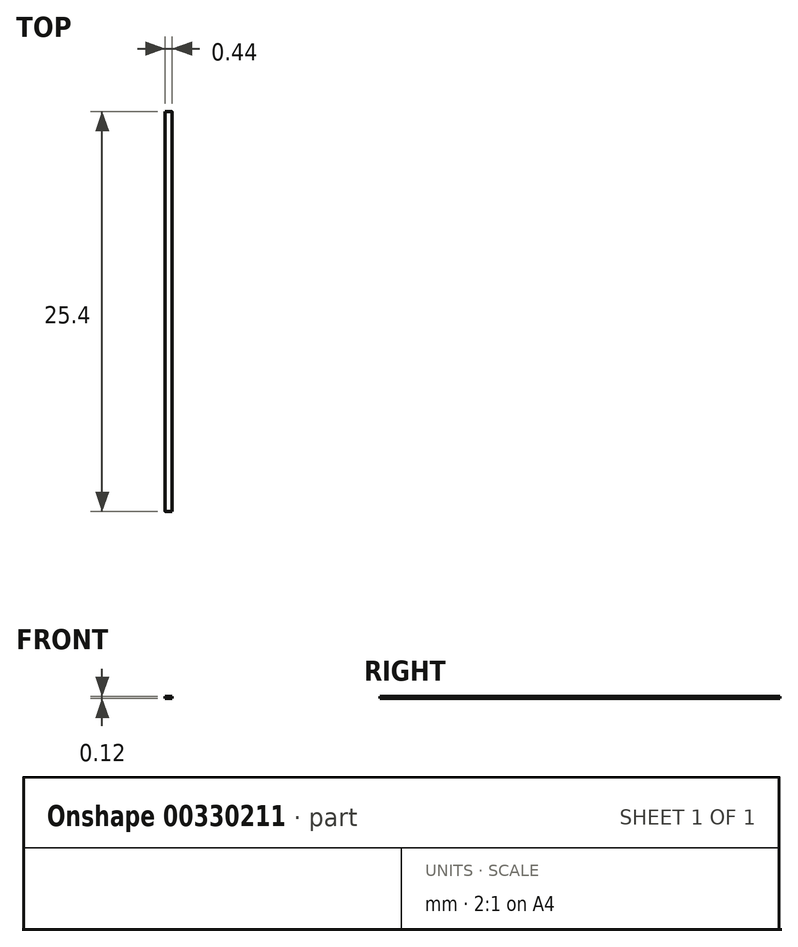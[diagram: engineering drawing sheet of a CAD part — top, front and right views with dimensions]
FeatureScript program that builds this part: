
annotation { "Feature Type Name" : "Feature", "Feature Type Description" : "" }
export const myFeature = defineFeature(function(context is Context, id is Id, definition is map)
    precondition{}
    {
        {
            var Q0;
            Q0=qCreatedBy(makeId("Front.planeOp"),FACE);
            var sketch = newSketch(context, id + "F0", { "sketchPlane" : qUnion([Q0])});
            skLineSegment(sketch, "E0.bottom", {"start": v(0.22, -0.06) * mm, "end": v(-0.22, -0.06) * mm});
            skLineSegment(sketch, "E0.top", {"start": v(0.22, 0.06) * mm, "end": v(-0.22, 0.06) * mm});
            skLineSegment(sketch, "E0.left", {"start": v(0.22, -0.06) * mm, "end": v(0.22, 0.06) * mm});
            skLineSegment(sketch, "E0.right", {"start": v(-0.22, -0.06) * mm, "end": v(-0.22, 0.06) * mm});
            skPoint(sketch, "E0.middle", {"position": v(0, 0) * mm});
            skArc(sketch, "E1", {"start": v(0.22, -0.06) * mm, "mid": v(0.22, 0) * mm, "end": v(0.22, 0.06) * mm});
            skArc(sketch, "E2.MirrorCS", {"start": v(-0.22, -0.06) * mm, "mid": v(-0.22, 0) * mm, "end": v(-0.22, 0.06) * mm});
            skSolve(sketch);
        }
        {
            var Q0;
            Q0=makeQuery(id+"F0.imprint","IMPRINT",FACE,{"disambiguationData":[TD([[makeQuery(id+"F0.imprint","IMPRINT",EDGE,{"derivedFrom":sQuery(id+"F0.wireOp",EDGE,"E0.bottom")}),-1.0]])]});
            var Q1;
            Q1=makeQuery(id+"F0.imprint","IMPRINT",FACE,{"disambiguationData":[TD([[makeQuery(id+"F0.imprint","IMPRINT",EDGE,{"derivedFrom":sQuery(id+"F0.wireOp",EDGE,"E0.left")}),-1.0]])]});
            var Q2;
            Q2=makeQuery(id+"F0.imprint","IMPRINT",FACE,{"disambiguationData":[TD([[makeQuery(id+"F0.imprint","IMPRINT",EDGE,{"derivedFrom":sQuery(id+"F0.wireOp",EDGE,"E0.right")}),1.0]])]});
            extrude(context, id + "F1", {"entities" : qUnion([Q0, Q1, Q2]), "depth" : 25.4 * mm});
        }
    });
